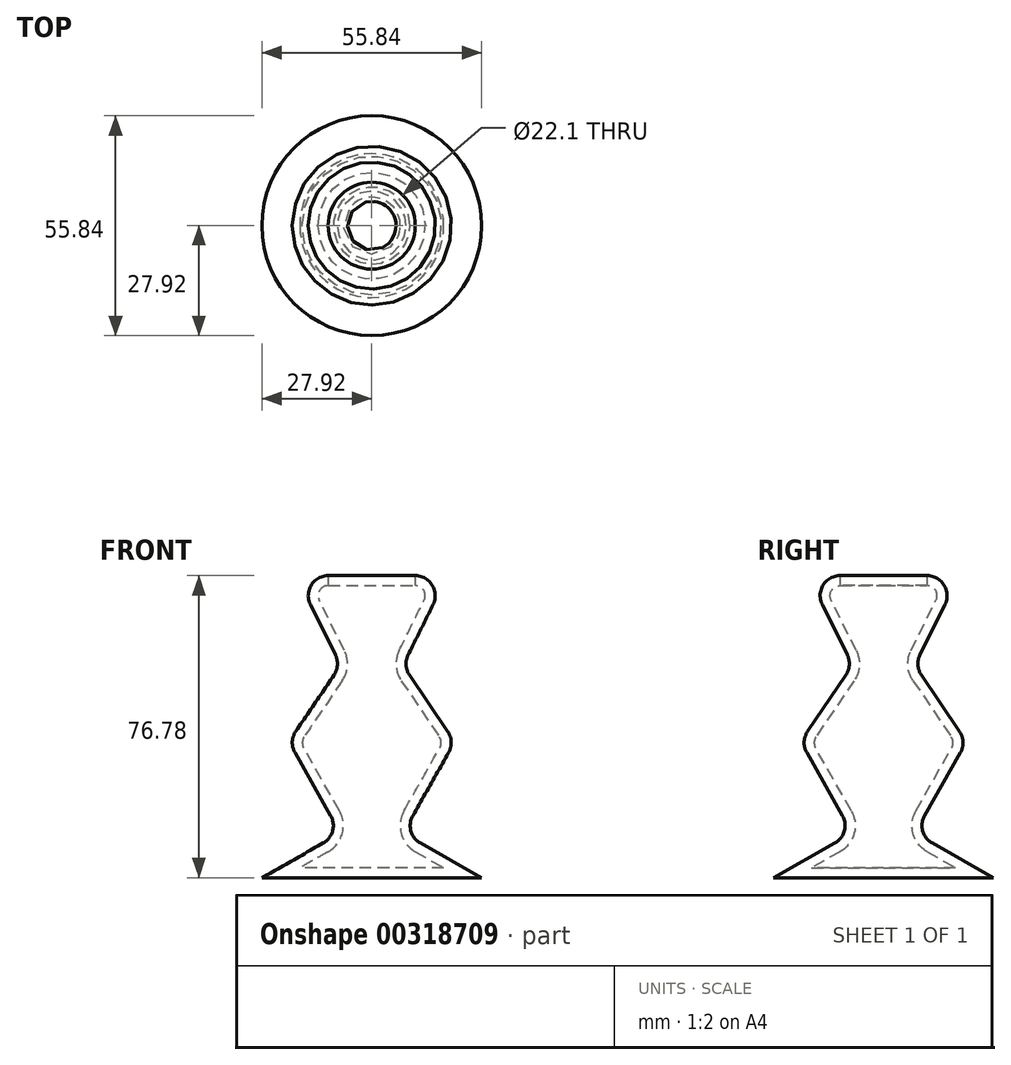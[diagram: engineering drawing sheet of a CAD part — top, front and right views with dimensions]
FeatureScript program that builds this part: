
annotation { "Feature Type Name" : "Feature", "Feature Type Description" : "" }
export const myFeature = defineFeature(function(context is Context, id is Id, definition is map)
    precondition{}
    {
        {
            var Q0;
            Q0=qCreatedBy(makeId("Front.planeOp"),FACE);
            var sketch = newSketch(context, id + "F0", { "sketchPlane" : qUnion([Q0])});
            skLineSegment(sketch, "E0", {"start": v(0, -76.78) * mm, "end": v(-27.92, -76.78) * mm});
            skLineSegment(sketch, "E1", {"start": v(-27.92, -76.78) * mm, "end": v(-7.92, -65.46) * mm});
            skLineSegment(sketch, "E2", {"start": v(-7.92, -65.46) * mm, "end": v(-21.08, -42.2) * mm});
            skLineSegment(sketch, "E3", {"start": v(-21.08, -42.2) * mm, "end": v(-7.92, -22.83) * mm});
            skLineSegment(sketch, "E4", {"start": v(-7.92, -22.83) * mm, "end": v(-19.24, 0) * mm});
            skLineSegment(sketch, "E5", {"start": v(-19.24, 0) * mm, "end": v(0, 0) * mm});
            skLineSegment(sketch, "E6", {"start": v(0, 0) * mm, "end": v(0, -76.78) * mm});
            skSolve(sketch);
        }
        {
            var Q0;
            Q0 = qSketchRegion(id + "F0", true);
            var Q1;
            Q1=sQuery(id+"F0.wireOp",EDGE,"E6");
            revolve(context, id + "F1", {"entities" : qUnion([Q0]), "axis" : qUnion([Q1]), "revolveType" : RevolveType.FULL});
        }
        {
            var Q0;
            Q0=makeQuery(id+"F1.opRevolve","SWEPT_EDGE",EDGE,{"disambiguationData":[OSD([sQuery(id+"F0.wireOp",EDGE,"E2"),sQuery(id+"F0.wireOp",EDGE,"E3")])]});
            var Q1;
            Q1=makeQuery(id+"F1.opRevolve","SWEPT_EDGE",EDGE,{"disambiguationData":[OSD([sQuery(id+"F0.wireOp",EDGE,"E3"),sQuery(id+"F0.wireOp",EDGE,"E4")])]});
            var Q2;
            Q2=makeQuery(id+"F1.opRevolve","SWEPT_FACE",FACE,{"disambiguationData":[OSD([sQuery(id+"F0.wireOp",EDGE,"E4")])]});
            var Q3;
            Q3=makeQuery(id+"F1.opRevolve","SWEPT_EDGE",EDGE,{"disambiguationData":[OSD([sQuery(id+"F0.wireOp",EDGE,"E1"),sQuery(id+"F0.wireOp",EDGE,"E2")])]});
            fillet(context, id + "F2", {"entities" : qUnion([Q0, Q1, Q2, Q3]), "radius" : 5.08 * mm, "tangentPropagation" : true, "allowEdgeOverflow" : false});
        }
        {
            var Q0;
            Q0=makeQuery(id+"F1.opRevolve","SWEPT_FACE",FACE,{"disambiguationData":[OSD([sQuery(id+"F0.wireOp",EDGE,"E5")])]});
            shell(context, id + "F3", {"entities" : qUnion([Q0]), "thickness" : 2.54 * mm});
        }
    });
